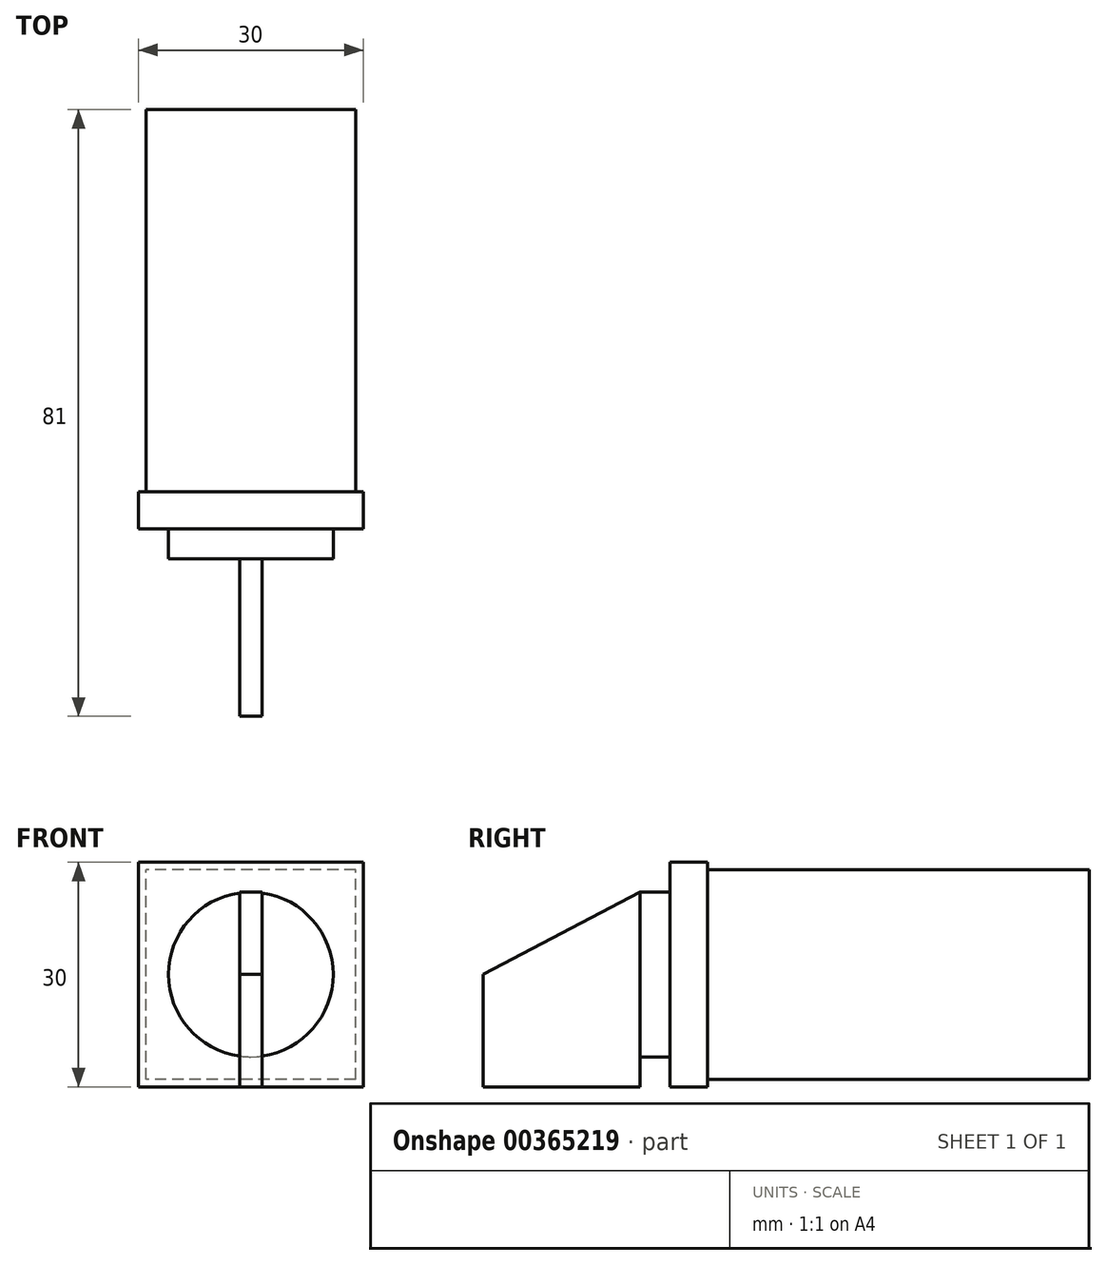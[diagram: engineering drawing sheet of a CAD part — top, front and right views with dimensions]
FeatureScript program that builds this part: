
annotation { "Feature Type Name" : "Feature", "Feature Type Description" : "" }
export const myFeature = defineFeature(function(context is Context, id is Id, definition is map)
    precondition{}
    {
        {
            var Q0;
            Q0=qCreatedBy(makeId("Front.planeOp"),FACE);
            var sketch = newSketch(context, id + "F0", { "sketchPlane" : qUnion([Q0])});
            skLineSegment(sketch, "E0.bottom", {"start": v(14, -14) * mm, "end": v(-14, -14) * mm});
            skLineSegment(sketch, "E0.top", {"start": v(14, 14) * mm, "end": v(-14, 14) * mm});
            skLineSegment(sketch, "E0.left", {"start": v(14, -14) * mm, "end": v(14, 14) * mm});
            skLineSegment(sketch, "E0.right", {"start": v(-14, -14) * mm, "end": v(-14, 14) * mm});
            skPoint(sketch, "E0.middle", {"position": v(0, 0) * mm});
            skSolve(sketch);
        }
        {
            var Q0;
            Q0 = qSketchRegion(id + "F0", true);
            extrude(context, id + "F1", {"entities" : qUnion([Q0]), "oppositeDirection" : true, "depth" : 51 * mm});
        }
        {
            var Q0;
            Q0=qCreatedBy(makeId("Front.planeOp"),FACE);
            var sketch = newSketch(context, id + "F2", { "sketchPlane" : qUnion([Q0])});
            skLineSegment(sketch, "E1.bottom", {"start": v(15, -15) * mm, "end": v(-15, -15) * mm});
            skLineSegment(sketch, "E1.top", {"start": v(15, 15) * mm, "end": v(-15, 15) * mm});
            skLineSegment(sketch, "E1.left", {"start": v(15, -15) * mm, "end": v(15, 15) * mm});
            skLineSegment(sketch, "E1.right", {"start": v(-15, -15) * mm, "end": v(-15, 15) * mm});
            skPoint(sketch, "E1.middle", {"position": v(0, 0) * mm});
            skSolve(sketch);
        }
        {
            var Q0;
            Q0 = qSketchRegion(id + "F2", true);
            extrude(context, id + "F3", {"entities" : qUnion([Q0]), "operationType" : NewBodyOperationType.ADD, "depth" : 5 * mm});
        }
        {
            var Q0;
            Q0=makeQuery(id+"F3.opExtrude","CAP_FACE",FACE,{"disambiguationData":[OSD([sQuery(id+"F2.wireOp",EDGE,"E1.bottom"),sQuery(id+"F2.wireOp",EDGE,"E1.top"),sQuery(id+"F2.wireOp",EDGE,"E1.left"),sQuery(id+"F2.wireOp",EDGE,"E1.right")])],"isStart":false});
            var sketch = newSketch(context, id + "F4", { "sketchPlane" : qUnion([Q0])});
            skCircle(sketch, "E2", {"center": v(0, 0) * mm, "radius": 11 * mm});
            skSolve(sketch);
        }
        {
            var Q0;
            Q0 = qSketchRegion(id + "F4", true);
            extrude(context, id + "F5", {"entities" : qUnion([Q0]), "operationType" : NewBodyOperationType.ADD, "depth" : 4 * mm});
        }
        {
            var Q0;
            Q0=makeQuery(id+"F5.opExtrude","CAP_FACE",FACE,{"disambiguationData":[OSD([sQuery(id+"F4.wireOp",EDGE,"E2")])],"isStart":false});
            var sketch = newSketch(context, id + "F6", { "sketchPlane" : qUnion([Q0])});
            skLineSegment(sketch, "E3.0", {"start": v(15, -15) * mm, "end": v(-15, -15) * mm, "construction": true});
            skLineSegment(sketch, "E4.bottom", {"start": v(1.5, -15) * mm, "end": v(-1.5, -15) * mm, "construction": true});
            skLineSegment(sketch, "E4.top", {"start": v(1.5, 15) * mm, "end": v(-1.5, 15) * mm, "construction": true});
            skLineSegment(sketch, "E4.left", {"start": v(1.5, -15) * mm, "end": v(1.5, 15) * mm, "construction": true});
            skLineSegment(sketch, "E4.right", {"start": v(-1.5, -15) * mm, "end": v(-1.5, 15) * mm, "construction": true});
            skPoint(sketch, "E4.middle", {"position": v(0, 0) * mm});
            skLineSegment(sketch, "E5.bottom", {"start": v(-1.5, -15) * mm, "end": v(1.5, -15) * mm});
            skLineSegment(sketch, "E5.top", {"start": v(-1.5, 0) * mm, "end": v(1.5, 0) * mm});
            skLineSegment(sketch, "E5.left", {"start": v(-1.5, -15) * mm, "end": v(-1.5, 0) * mm});
            skLineSegment(sketch, "E5.right", {"start": v(1.5, -15) * mm, "end": v(1.5, 0) * mm});
            skSolve(sketch);
        }
        {
            var Q0;
            Q0 = qSketchRegion(id + "F6", true);
            extrude(context, id + "F7", {"entities" : qUnion([Q0]), "operationType" : NewBodyOperationType.ADD, "depth" : 21 * mm});
        }
        {
            var Q0;
            Q0=makeQuery(id+"F7.opExtrude","SWEPT_FACE",FACE,{"disambiguationData":[OSD([sQuery(id+"F6.wireOp",EDGE,"E5.right")])]});
            var sketch = newSketch(context, id + "F8", { "sketchPlane" : qUnion([Q0])});
            skLineSegment(sketch, "E6.0", {"start": v(-9, -10.9) * mm, "end": v(-9, 11) * mm, "construction": true});
            skLineSegment(sketch, "E7.0", {"start": v(-30, 0) * mm, "end": v(-9, 0) * mm, "construction": true});
            skLineSegment(sketch, "E8", {"start": v(-30, 0) * mm, "end": v(-9, 11) * mm});
            skLineSegment(sketch, "E9", {"start": v(-9, 0) * mm, "end": v(-9, 11) * mm});
            skLineSegment(sketch, "E10", {"start": v(-30, 0) * mm, "end": v(-9, 0) * mm});
            skSolve(sketch);
        }
        {
            var Q0;
            Q0=makeQuery(id+"F8.imprint","IMPRINT",FACE,{"disambiguationData":[TD([[makeQuery(id+"F8.imprint","IMPRINT",EDGE,{"derivedFrom":sQuery(id+"F8.wireOp",EDGE,"E8")}),-1.0]])]});
            extrude(context, id + "F9", {"entities" : qUnion([Q0]), "operationType" : NewBodyOperationType.ADD, "oppositeDirection" : true, "depth" : 3 * mm});
        }
    });
